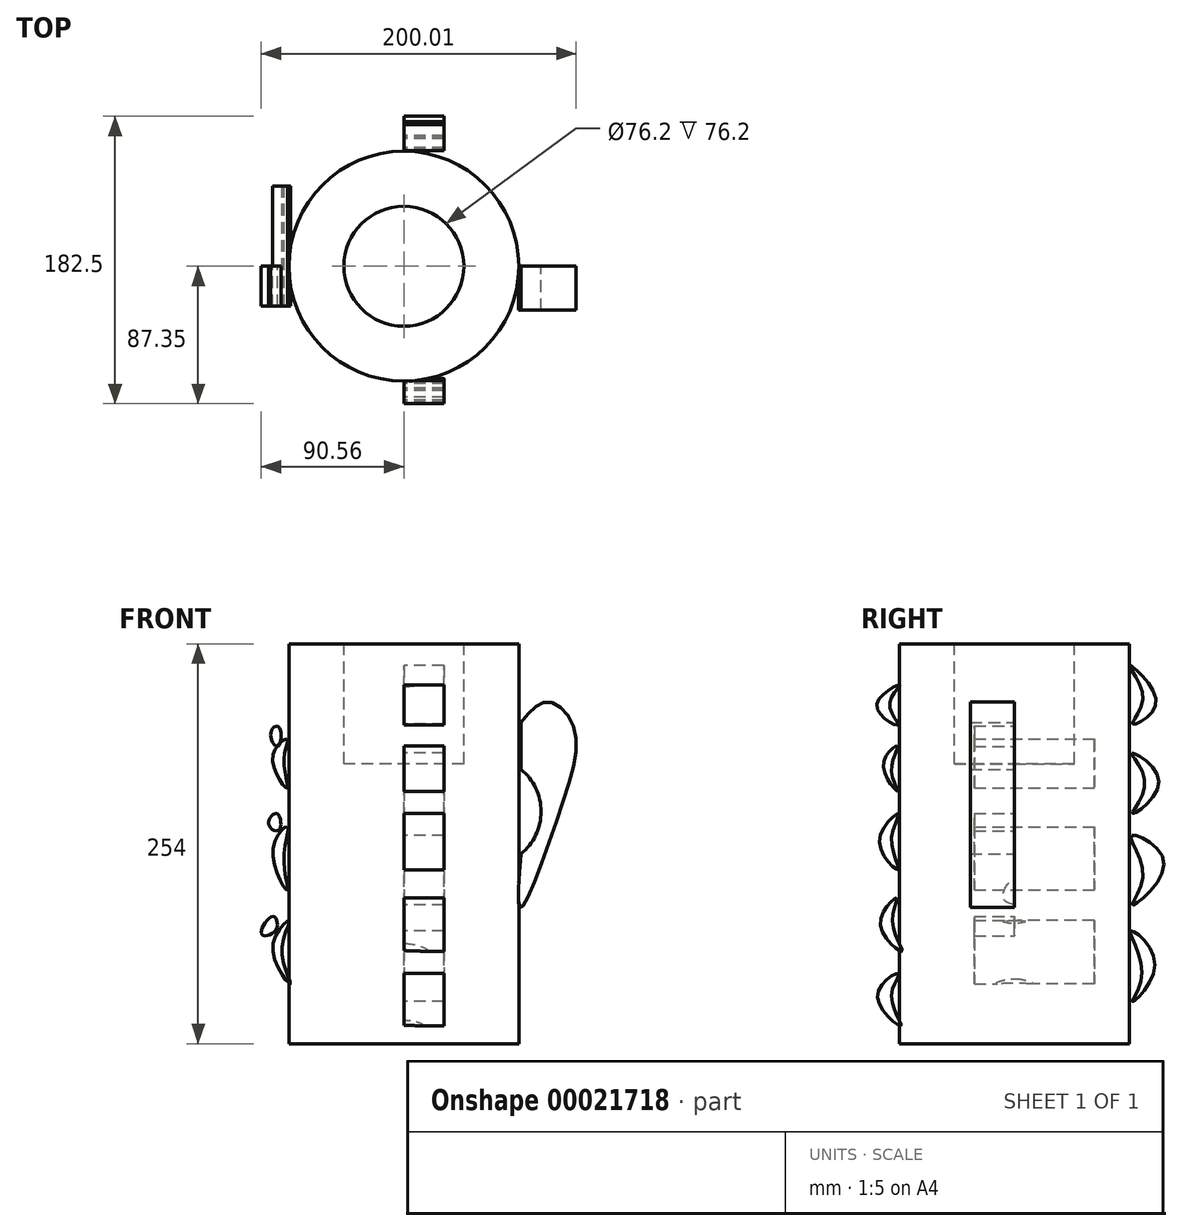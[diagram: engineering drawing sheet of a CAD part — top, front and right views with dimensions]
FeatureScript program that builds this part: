
annotation { "Feature Type Name" : "Feature", "Feature Type Description" : "" }
export const myFeature = defineFeature(function(context is Context, id is Id, definition is map)
    precondition{}
    {
        {
            var Q0;
            Q0=qCreatedBy(makeId("Top.planeOp"),FACE);
            var sketch = newSketch(context, id + "F0", { "sketchPlane" : qUnion([Q0])});
            skCircle(sketch, "E0", {"center": v(0, 0) * mm, "radius": 73.03 * mm});
            skSolve(sketch);
        }
        {
            var Q0;
            Q0 = qSketchRegion(id + "F0", true);
            var Q1;
            Q1 = qSketchRegion(id + "F5AdWluwrxAyDaj_0", true);
            extrude(context, id + "F1", {"entities" : qUnion([Q0, Q1]), "depth" : 254 * mm});
        }
        {
            var Q0;
            Q0=makeQuery(id+"F1.opExtrude","CAP_FACE",FACE,{"disambiguationData":[OSD([sQuery(id+"F0.wireOp",EDGE,"E0")])],"isStart":false});
            var sketch = newSketch(context, id + "F2", { "sketchPlane" : qUnion([Q0])});
            skCircle(sketch, "E1", {"center": v(0, 0) * mm, "radius": 38.1 * mm});
            skSolve(sketch);
        }
        {
            var Q0;
            Q0=makeQuery(id+"F2.imprint","IMPRINT",FACE,{"disambiguationData":[TD([[makeQuery(id+"F2.imprint","IMPRINT",EDGE,{"derivedFrom":sQuery(id+"F2.wireOp",EDGE,"E1")}),1.0]])]});
            extrude(context, id + "F3", {"entities" : qUnion([Q0]), "operationType" : NewBodyOperationType.REMOVE, "oppositeDirection" : true, "depth" : 76.2 * mm});
        }
        {
            var Q0;
            Q0=qCreatedBy(makeId("Front.planeOp"),FACE);
            var sketch = newSketch(context, id + "F4", { "sketchPlane" : qUnion([Q0])});
            skFitSpline(sketch, "E2", {"points": [v(74.3, 204) * mm, v(91.32, 217.2) * mm, v(107.8, 201.26) * mm, v(98.47, 145.77) * mm, v(74.3, 86.42) * mm, v(74.3, 120.5) * mm], "startDerivative": vector(107.98, 131.62) * mm, "endDerivative": vector(21.9, 271.59) * mm});
            skLineSegment(sketch, "E3", {"start": v(74.3, 204) * mm, "end": v(74.3, 174.34) * mm});
            skArc(sketch, "E4", {"start": v(74.3, 120.5) * mm, "mid": v(87.14, 147.41) * mm, "end": v(74.3, 174.34) * mm});
            skSolve(sketch);
        }
        {
            var Q0;
            Q0 = qSketchRegion(id + "F4", true);
            extrude(context, id + "F5", {"entities" : qUnion([Q0]), "operationType" : NewBodyOperationType.ADD, "depth" : 27.94 * mm});
        }
        {
            var Q0;
            Q0=qCreatedBy(makeId("Right.planeOp"),FACE);
            var sketch = newSketch(context, id + "F6", { "sketchPlane" : qUnion([Q0])});
            skFitSpline(sketch, "E5", {"points": [v(-72.66, 227.96) * mm, v(-87.35, 214.55) * mm, v(-73.94, 202.41) * mm, v(-79.05, 215.83) * mm, v(-72.66, 227.96) * mm]});
            skSolve(sketch);
        }
        {
            var Q0;
            Q0=makeQuery(id+"F6.imprint","IMPRINT",FACE,{"disambiguationData":[TD([[makeQuery(id+"F6.imprint","IMPRINT",EDGE,{"derivedFrom":sQuery(id+"F6.wireOp",EDGE,"E5")}),1.0]])]});
            var Q1;
            Q1=sQuery(id+"F6.wireOp",EDGE,"E5");
            extrude(context, id + "F7", {"entities" : qUnion([Q0]), "operationType" : NewBodyOperationType.ADD, "surfaceEntities" : qUnion([Q1]), "depth" : 25.4 * mm});
        }
        {
            var Q0;
            Q0=qCreatedBy(makeId("Right.planeOp"),FACE);
            var sketch = newSketch(context, id + "F8", { "sketchPlane" : qUnion([Q0])});
            skFitSpline(sketch, "E6", {"points": [v(-74.14, 189) * mm, v(-83.08, 177.5) * mm, v(-74.14, 160.26) * mm, v(-77.97, 174.31) * mm, v(-74.14, 189) * mm]});
            skFitSpline(sketch, "E7", {"points": [v(-73.5, 146.21) * mm, v(-85.63, 128.33) * mm, v(-73.5, 110.44) * mm, v(-77.97, 128.97) * mm, v(-73.5, 146.21) * mm]});
            skFitSpline(sketch, "E8", {"points": [v(-74.78, 92.56) * mm, v(-85, 75.96) * mm, v(-71.58, 58.71) * mm, v(-77.33, 76.6) * mm, v(-74.78, 92.56) * mm]});
            skFitSpline(sketch, "E9", {"points": [v(-73.5, 44.66) * mm, v(-86.91, 30.61) * mm, v(-72.22, 11.45) * mm, v(-77.97, 29.97) * mm, v(-73.5, 44.66) * mm]});
            skFitSpline(sketch, "E10", {"points": [v(73.4, 240.1) * mm, v(90, 216.47) * mm, v(75.31, 203.05) * mm, v(81.7, 219.66) * mm, v(73.4, 240.1) * mm]});
            skFitSpline(sketch, "E11", {"points": [v(74.67, 184.53) * mm, v(91.92, 166.65) * mm, v(75.31, 146.21) * mm, v(82.98, 166) * mm, v(74.67, 184.53) * mm]});
            skFitSpline(sketch, "E12", {"points": [v(74.67, 132.16) * mm, v(95.11, 114.92) * mm, v(75.31, 88.1) * mm, v(81.7, 107.9) * mm, v(74.67, 132.16) * mm]});
            skFitSpline(sketch, "E13", {"points": [v(74.03, 71.49) * mm, v(89.36, 51.05) * mm, v(75.31, 26.78) * mm, v(81.06, 45.3) * mm, v(74.03, 71.49) * mm]});
            skSolve(sketch);
        }
        {
            var Q0;
            Q0=makeQuery(id+"F8.imprint","IMPRINT",FACE,{"disambiguationData":[TD([[makeQuery(id+"F8.imprint","IMPRINT",EDGE,{"derivedFrom":sQuery(id+"F8.wireOp",EDGE,"E6")}),1.0]])]});
            var Q1;
            Q1=makeQuery(id+"F8.imprint","IMPRINT",FACE,{"disambiguationData":[TD([[makeQuery(id+"F8.imprint","IMPRINT",EDGE,{"derivedFrom":sQuery(id+"F8.wireOp",EDGE,"E7")}),1.0]])]});
            var Q2;
            Q2=makeQuery(id+"F8.imprint","IMPRINT",FACE,{"disambiguationData":[TD([[makeQuery(id+"F8.imprint","IMPRINT",EDGE,{"derivedFrom":sQuery(id+"F8.wireOp",EDGE,"E8")}),1.0]])]});
            var Q3;
            Q3=makeQuery(id+"F8.imprint","IMPRINT",FACE,{"disambiguationData":[TD([[makeQuery(id+"F8.imprint","IMPRINT",EDGE,{"derivedFrom":sQuery(id+"F8.wireOp",EDGE,"E9")}),1.0]])]});
            var Q4;
            Q4=makeQuery(id+"F8.imprint","IMPRINT",FACE,{"disambiguationData":[TD([[makeQuery(id+"F8.imprint","IMPRINT",EDGE,{"derivedFrom":sQuery(id+"F8.wireOp",EDGE,"E10")}),-1.0]])]});
            var Q5;
            Q5=makeQuery(id+"F8.imprint","IMPRINT",FACE,{"disambiguationData":[TD([[makeQuery(id+"F8.imprint","IMPRINT",EDGE,{"derivedFrom":sQuery(id+"F8.wireOp",EDGE,"E11")}),-1.0]])]});
            var Q6;
            Q6=makeQuery(id+"F8.imprint","IMPRINT",FACE,{"disambiguationData":[TD([[makeQuery(id+"F8.imprint","IMPRINT",EDGE,{"derivedFrom":sQuery(id+"F8.wireOp",EDGE,"E12")}),-1.0]])]});
            var Q7;
            Q7=makeQuery(id+"F8.imprint","IMPRINT",FACE,{"disambiguationData":[TD([[makeQuery(id+"F8.imprint","IMPRINT",EDGE,{"derivedFrom":sQuery(id+"F8.wireOp",EDGE,"E13")}),-1.0]])]});
            extrude(context, id + "F9", {"entities" : qUnion([Q0, Q1, Q2, Q3, Q4, Q5, Q6, Q7]), "operationType" : NewBodyOperationType.ADD, "depth" : 25.4 * mm});
        }
        {
            var Q0;
            Q0=qCreatedBy(makeId("Front.planeOp"),FACE);
            var sketch = newSketch(context, id + "F10", { "sketchPlane" : qUnion([Q0])});
            skFitSpline(sketch, "E14", {"points": [v(-74.15, 193.4) * mm, v(-83.22, 182.4) * mm, v(-74.15, 162.32) * mm, v(-76.1, 181.1) * mm, v(-74.15, 193.4) * mm]});
            skFitSpline(sketch, "E15", {"points": [v(-74.15, 137.7) * mm, v(-83.22, 122.81) * mm, v(-74.15, 97.55) * mm, v(-76.1, 117.63) * mm, v(-74.15, 137.7) * mm]});
            skFitSpline(sketch, "E16", {"points": [v(-72.86, 78.12) * mm, v(-83.22, 61.29) * mm, v(-72.21, 37.97) * mm, v(-77.4, 59.34) * mm, v(-72.86, 78.12) * mm]});
            skSolve(sketch);
        }
        {
            var Q0;
            Q0=makeQuery(id+"F10.imprint","IMPRINT",FACE,{"disambiguationData":[TD([[makeQuery(id+"F10.imprint","IMPRINT",EDGE,{"derivedFrom":sQuery(id+"F10.wireOp",EDGE,"E14")}),1.0]])]});
            var Q1;
            Q1=makeQuery(id+"F10.imprint","IMPRINT",FACE,{"disambiguationData":[TD([[makeQuery(id+"F10.imprint","IMPRINT",EDGE,{"derivedFrom":sQuery(id+"F10.wireOp",EDGE,"E15")}),1.0]])]});
            var Q2;
            Q2=makeQuery(id+"F10.imprint","IMPRINT",FACE,{"disambiguationData":[TD([[makeQuery(id+"F10.imprint","IMPRINT",EDGE,{"derivedFrom":sQuery(id+"F10.wireOp",EDGE,"E16")}),1.0]])]});
            extrude(context, id + "F11", {"entities" : qUnion([Q0, Q1, Q2]), "operationType" : NewBodyOperationType.ADD, "depth" : 25.4 * mm, "hasSecondDirection" : true, "secondDirectionOppositeDirection" : true, "secondDirectionDepth" : 50.8 * mm});
        }
        {
            var Q0;
            Q0=qCreatedBy(makeId("Front.planeOp"),FACE);
            var sketch = newSketch(context, id + "F12", { "sketchPlane" : qUnion([Q0])});
            skFitSpline(sketch, "E17", {"points": [v(-79.98, 188.87) * mm, v(-79.34, 201.17) * mm, v(-84.52, 197.29) * mm, v(-79.98, 188.87) * mm]});
            skFitSpline(sketch, "E18", {"points": [v(-79.34, 135.76) * mm, v(-80.63, 146.13) * mm, v(-85.81, 139.65) * mm, v(-79.34, 135.76) * mm]});
            skFitSpline(sketch, "E19", {"points": [v(-81.28, 72.3) * mm, v(-83.22, 80.71) * mm, v(-90.35, 69.7) * mm, v(-81.28, 72.3) * mm]});
            skSolve(sketch);
        }
        {
            var Q0;
            Q0=makeQuery(id+"F12.imprint","IMPRINT",FACE,{"disambiguationData":[TD([[makeQuery(id+"F12.imprint","IMPRINT",EDGE,{"derivedFrom":sQuery(id+"F12.wireOp",EDGE,"E17")}),1.0]])]});
            var Q1;
            Q1=makeQuery(id+"F12.imprint","IMPRINT",FACE,{"disambiguationData":[TD([[makeQuery(id+"F12.imprint","IMPRINT",EDGE,{"derivedFrom":sQuery(id+"F12.wireOp",EDGE,"E19")}),1.0]])]});
            var Q2;
            Q2=makeQuery(id+"F12.imprint","IMPRINT",FACE,{"disambiguationData":[TD([[makeQuery(id+"F12.imprint","IMPRINT",EDGE,{"derivedFrom":sQuery(id+"F12.wireOp",EDGE,"E18")}),1.0]])]});
            extrude(context, id + "F13", {"entities" : qUnion([Q0, Q1, Q2]), "depth" : 25.4 * mm});
        }
    });
